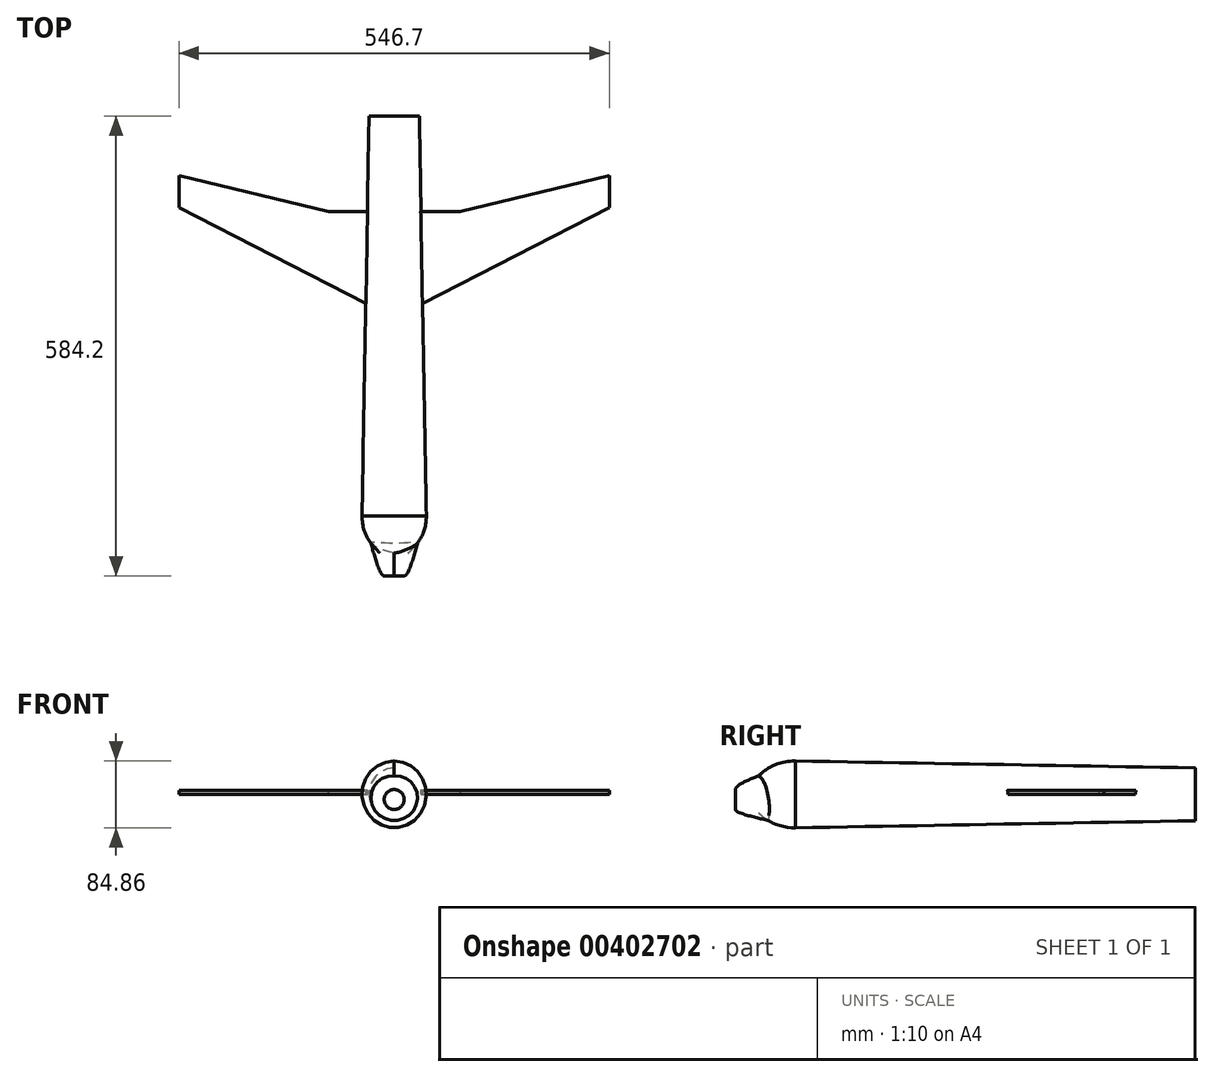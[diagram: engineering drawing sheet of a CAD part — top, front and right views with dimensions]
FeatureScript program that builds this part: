
annotation { "Feature Type Name" : "Feature", "Feature Type Description" : "" }
export const myFeature = defineFeature(function(context is Context, id is Id, definition is map)
    precondition{}
    {
        {
            var Q0;
            Q0=qCreatedBy(makeId("Front.planeOp"),FACE);
            var sketch = newSketch(context, id + "F0", { "sketchPlane" : qUnion([Q0])});
            skEllipse(sketch, "E0", {"center": v(0, 0) * mm, "majorRadius": 40.88 * mm, "minorRadius": 42.43 * mm, "majorAxis": v(1, 0)});
            skSolve(sketch);
        }
        {
            var Q0;
            Q0=qCreatedBy(makeId("Front.planeOp"),FACE);
            cPlane(context, id + "F1", {"entities" : qUnion([Q0]), "cplaneType" : CPlaneType.OFFSET, "offset" : 50.8 * mm, "width" : 152.4 * mm, "height" : 152.4 * mm});
        }
        {
            var Q0;
            Q0=qCreatedBy(id+"F1.planeOp",FACE);
            var sketch = newSketch(context, id + "F2", { "sketchPlane" : qUnion([Q0])});
            skEllipse(sketch, "E1", {"center": v(0, 0) * mm, "majorRadius": 14.47 * mm, "minorRadius": 20.57 * mm, "majorAxis": v(1, 0)});
            skSolve(sketch);
        }
        {
            var Q0;
            Q0=makeQuery(id+"F0.imprint","IMPRINT",FACE,{"disambiguationData":[TD([[makeQuery(id+"F0.imprint","IMPRINT",EDGE,{"derivedFrom":sQuery(id+"F0.wireOp",EDGE,"E0")}),1.0]])]});
            var Q1;
            Q1=makeQuery(id+"F2.imprint","IMPRINT",FACE,{"disambiguationData":[TD([[makeQuery(id+"F2.imprint","IMPRINT",EDGE,{"derivedFrom":sQuery(id+"F2.wireOp",EDGE,"E1")}),1.0]])]});
            loft(context, id + "F3", {"startCondition" : LoftEndDerivativeType.NORMAL_TO_PROFILE, "startMagnitude" : 2, "endCondition" : LoftEndDerivativeType.NORMAL_TO_PROFILE, "endMagnitude" : 0.2, "sheetProfilesArray" : [{ "sheetProfileEntities" : qUnion([Q0]) }, { "sheetProfileEntities" : qUnion([Q1]) }]});
        }
        {
            var Q0;
            Q0=makeQuery(id+"F3.opLoft","CAP_FACE",FACE,{"disambiguationData":[OSD([makeQuery(id+"F2.imprint","IMPRINT",FACE,{"disambiguationData":[TD([[makeQuery(id+"F2.imprint","IMPRINT",EDGE,{"derivedFrom":sQuery(id+"F2.wireOp",EDGE,"E1")}),1.0]])]})])],"isStart":true});
            cPlane(context, id + "F4", {"entities" : qUnion([Q0]), "cplaneType" : CPlaneType.OFFSET, "offset" : 25.4 * mm, "width" : 152.4 * mm, "height" : 152.4 * mm});
        }
        {
            var Q0;
            Q0=qCreatedBy(id+"F4.planeOp",FACE);
            var sketch = newSketch(context, id + "F5", { "sketchPlane" : qUnion([Q0])});
            skCircle(sketch, "E2", {"center": v(0, -6.54) * mm, "radius": 12.7 * mm});
            skSolve(sketch);
        }
        {
            var Q0;
            Q0=makeQuery(id+"F3.opLoft","CAP_FACE",FACE,{"disambiguationData":[OSD([makeQuery(id+"F2.imprint","IMPRINT",FACE,{"disambiguationData":[TD([[makeQuery(id+"F2.imprint","IMPRINT",EDGE,{"derivedFrom":sQuery(id+"F2.wireOp",EDGE,"E1")}),1.0]])]})])],"isStart":true});
            cPlane(context, id + "F6", {"entities" : qUnion([Q0]), "cplaneType" : CPlaneType.OFFSET, "offset" : 10.16 * mm, "oppositeDirection" : true, "width" : 152.4 * mm, "height" : 152.4 * mm});
        }
        {
            var Q0;
            Q0=makeQuery(id+"F0.imprint","IMPRINT",FACE,{"disambiguationData":[TD([[makeQuery(id+"F0.imprint","IMPRINT",EDGE,{"derivedFrom":sQuery(id+"F0.wireOp",EDGE,"E0")}),1.0]])]});
            var Q1;
            Q1=makeQuery(id+"F5.imprint","IMPRINT",FACE,{"disambiguationData":[TD([[makeQuery(id+"F5.imprint","IMPRINT",EDGE,{"derivedFrom":sQuery(id+"F5.wireOp",EDGE,"E2")}),1.0]])]});
            loft(context, id + "F7", {"operationType" : NewBodyOperationType.ADD, "startCondition" : LoftEndDerivativeType.TANGENT_TO_PROFILE, "startMagnitude" : 0.5, "endCondition" : LoftEndDerivativeType.TANGENT_TO_PROFILE, "endMagnitude" : 1, "sheetProfilesArray" : [{ "sheetProfileEntities" : qUnion([Q0]) }, { "sheetProfileEntities" : qUnion([Q1]) }]});
        }
        {
            var Q0;
            Q0=makeQuery(id+"F3.opLoft","CAP_FACE",FACE,{"disambiguationData":[OSD([makeQuery(id+"F0.imprint","IMPRINT",FACE,{"disambiguationData":[TD([[makeQuery(id+"F0.imprint","IMPRINT",EDGE,{"derivedFrom":sQuery(id+"F0.wireOp",EDGE,"E0")}),1.0]])]})])],"isStart":true});
            var sketch = newSketch(context, id + "F8", { "sketchPlane" : qUnion([Q0])});
            skSolve(sketch);
        }
        {
            var Q0;
            Q0=makeQuery(id+"F8.imprint","IMPRINT",FACE,{"disambiguationData":[TD([[makeQuery(id+"F8.imprint","IMPRINT",EDGE,{"derivedFrom":makeQuery(id+"F3.opLoft","MID_CAP_EDGE",EDGE,{"disambiguationData":[OSD([sQuery(id+"F0.wireOp",EDGE,"E0")])],"capPos":0.0})}),1.0]])]});
            extrude(context, id + "F9", {"entities" : qUnion([Q0]), "operationType" : NewBodyOperationType.ADD, "depth" : 508 * mm, "hasDraft" : true, "draftAngle" : 1 * degree, "draftPullDirection" : true});
        }
        {
            var Q0;
            Q0=qCreatedBy(makeId("Top.planeOp"),FACE);
            var sketch = newSketch(context, id + "F10", { "sketchPlane" : qUnion([Q0])});
            skLineSegment(sketch, "E3", {"start": v(227.23, 351.19) * mm, "end": v(227.23, 351.19) * mm});
            skLineSegment(sketch, "E4", {"start": v(227.23, 402.54) * mm, "end": v(227.23, 402.54) * mm});
            skLineSegment(sketch, "E5", {"start": v(83.61, 363.05) * mm, "end": v(83.61, 363.05) * mm});
            skLineSegment(sketch, "E6", {"start": v(0, 363.05) * mm, "end": v(0, 363.05) * mm});
            skPoint(sketch, "E7.start.orphan", {"position": v(0, 251.34) * mm});
            skLineSegment(sketch, "E8", {"start": v(0, 251.34) * mm, "end": v(273.33, 391.8) * mm});
            skLineSegment(sketch, "E9", {"start": v(273.33, 391.8) * mm, "end": v(273.33, 391.8) * mm});
            skLineSegment(sketch, "E10", {"start": v(273.33, 391.8) * mm, "end": v(273.33, 432.29) * mm});
            skLineSegment(sketch, "E11", {"start": v(273.33, 432.29) * mm, "end": v(83.61, 386.43) * mm});
            skLineSegment(sketch, "E12", {"start": v(83.61, 386.43) * mm, "end": v(83.61, 386.43) * mm});
            skLineSegment(sketch, "E13", {"start": v(83.61, 386.43) * mm, "end": v(0, 386.43) * mm});
            skLineSegment(sketch, "E14", {"start": v(0, 386.43) * mm, "end": v(0, 251.34) * mm});
            skLineSegment(sketch, "E15", {"start": v(0, 251.34) * mm, "end": v(0, 167.73) * mm, "construction": true});
            skLineSegment(sketch, "E16.MirrorCS", {"start": v(-273.33, 432.29) * mm, "end": v(-83.61, 386.43) * mm});
            skLineSegment(sketch, "E17.MirrorCS", {"start": v(0, 251.34) * mm, "end": v(-273.33, 391.8) * mm});
            skLineSegment(sketch, "E18.MirrorCS", {"start": v(-273.33, 391.8) * mm, "end": v(-273.33, 432.29) * mm});
            skLineSegment(sketch, "E19.MirrorCS", {"start": v(-83.61, 386.43) * mm, "end": v(0, 386.43) * mm});
            skSolve(sketch);
        }
        {
            var Q0;
            Q0 = qSketchRegion(id + "F10", true);
            extrude(context, id + "F11", {"entities" : qUnion([Q0]), "operationType" : NewBodyOperationType.ADD, "depth" : 5.08 * mm, "hasDraft" : true, "draftAngle" : 0.2 * degree});
        }
    });
